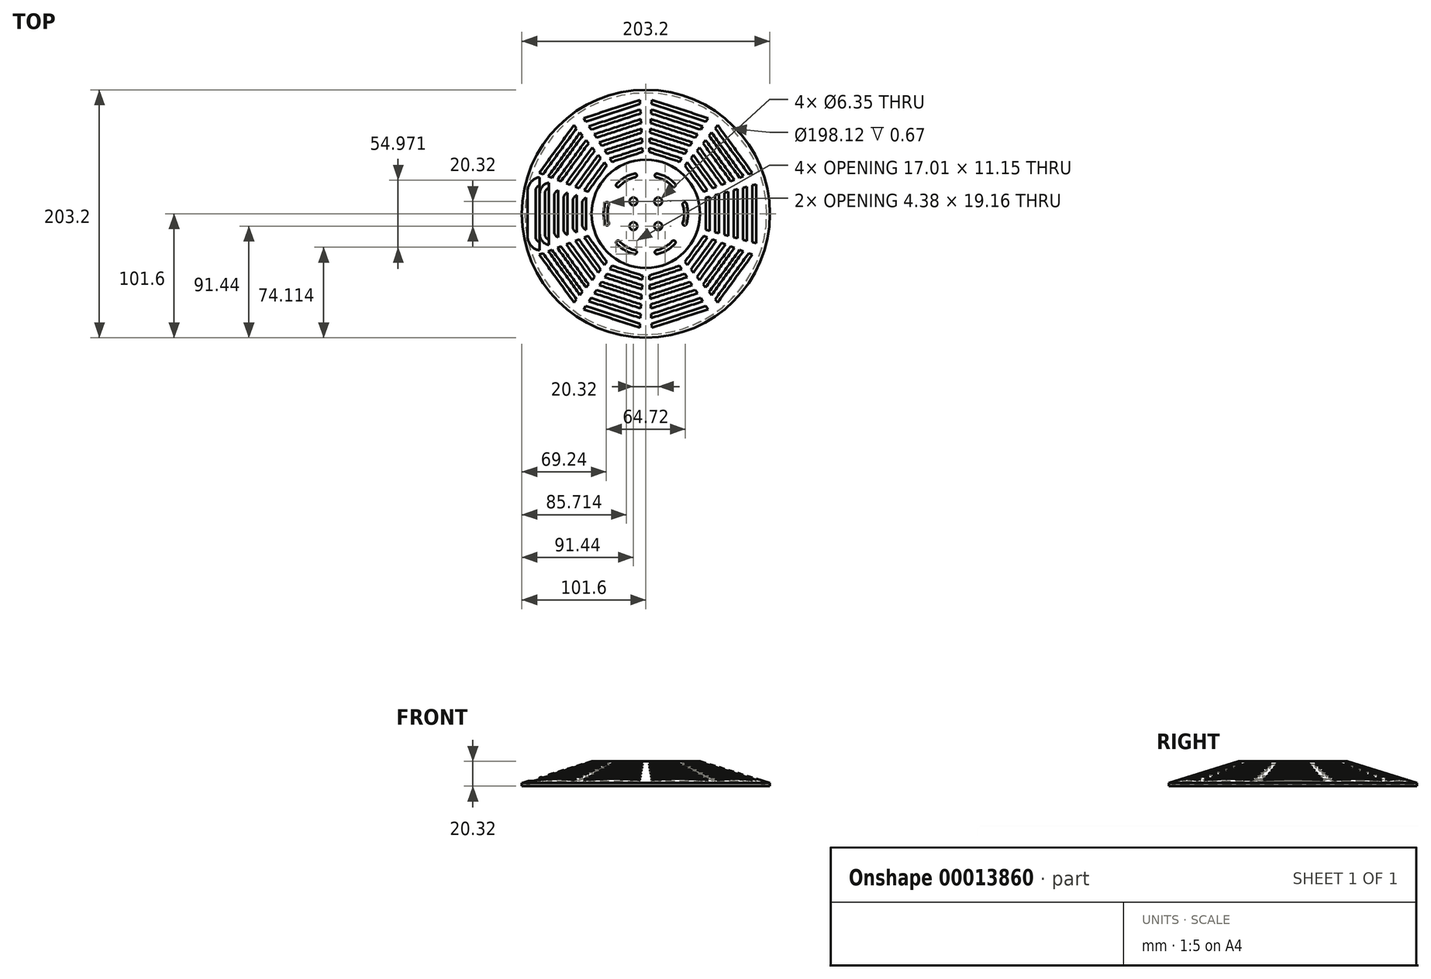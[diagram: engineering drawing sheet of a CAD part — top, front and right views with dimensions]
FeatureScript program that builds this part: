
annotation { "Feature Type Name" : "Feature", "Feature Type Description" : "" }
export const myFeature = defineFeature(function(context is Context, id is Id, definition is map)
    precondition{}
    {
        {
            var Q0;
            Q0=qCreatedBy(makeId("Front.planeOp"),FACE);
            var sketch = newSketch(context, id + "F0", { "sketchPlane" : qUnion([Q0])});
            skLineSegment(sketch, "E0", {"start": v(0, 0) * mm, "end": v(0, 20.32) * mm});
            skLineSegment(sketch, "E1", {"start": v(0, 20.32) * mm, "end": v(44.45, 20.32) * mm});
            skLineSegment(sketch, "E2", {"start": v(44.45, 20.32) * mm, "end": v(101.6, 2.54) * mm});
            skLineSegment(sketch, "E3", {"start": v(101.6, 2.54) * mm, "end": v(101.6, 0) * mm});
            skLineSegment(sketch, "E4", {"start": v(101.6, 0) * mm, "end": v(0, 0) * mm});
            skSolve(sketch);
        }
        {
            var Q0;
            Q0=makeQuery(id+"F0.imprint","IMPRINT",FACE,{"disambiguationData":[TD([[makeQuery(id+"F0.imprint","IMPRINT",EDGE,{"derivedFrom":sQuery(id+"F0.wireOp",EDGE,"E0")}),-1.0]])]});
            var Q1;
            Q1=sQuery(id+"F0.wireOp",EDGE,"E0");
            revolve(context, id + "F1", {"entities" : qUnion([Q0]), "axis" : qUnion([Q1]), "revolveType" : RevolveType.FULL});
        }
        {
            var Q0;
            Q0=makeQuery(id+"F1.opRevolve","SWEPT_FACE",FACE,{"disambiguationData":[OSD([sQuery(id+"F0.wireOp",EDGE,"E4")])]});
            shell(context, id + "F2", {"entities" : qUnion([Q0]), "thickness" : 2.54 * mm});
        }
        {
            var Q0;
            Q0=makeQuery(id+"F1.opRevolve","SWEPT_FACE",FACE,{"disambiguationData":[OSD([sQuery(id+"F0.wireOp",EDGE,"E1")])]});
            var sketch = newSketch(context, id + "F3", { "sketchPlane" : qUnion([Q0])});
            skArc(sketch, "E5", {"start": v(-30.23, 7.53) * mm, "mid": v(-31.38, 0) * mm, "end": v(-30.23, -7.53) * mm});
            skArc(sketch, "E6.0", {"start": v(-33.27, 8.47) * mm, "mid": v(-34.55, 0) * mm, "end": v(-33.27, -8.47) * mm});
            skArc(sketch, "E7", {"start": v(-33.27, -8.47) * mm, "mid": v(-31.28, -9.52) * mm, "end": v(-30.23, -7.53) * mm});
            skArc(sketch, "E8", {"start": v(-30.23, 7.53) * mm, "mid": v(-31.28, 9.52) * mm, "end": v(-33.27, 8.47) * mm});
            skSolve(sketch);
        }
        {
            var Q0;
            Q0=makeQuery(id+"F3.imprint","IMPRINT",FACE,{"disambiguationData":[TD([[makeQuery(id+"F3.imprint","IMPRINT",EDGE,{"derivedFrom":sQuery(id+"F3.wireOp",EDGE,"E5")}),-1.0]])]});
            extrude(context, id + "F4", {"entities" : qUnion([Q0]), "endBound" : BoundingType.THROUGH_ALL, "oppositeDirection" : true, "depth" : 25.4 * mm});
        }
        {
            var Q0;
            Q0=makeQuery(id+"F4.opExtrude","SWEPT_BODY",BODY,{"disambiguationData":[OSD([sQuery(id+"F3.wireOp",EDGE,"E5"),sQuery(id+"F3.wireOp",EDGE,"E6.0"),sQuery(id+"F3.wireOp",EDGE,"E7"),sQuery(id+"F3.wireOp",EDGE,"E8")])]});
            var Q1;
            Q1=makeQuery(id+"F1.opRevolve","SWEPT_EDGE",EDGE,{"disambiguationData":[OSD([sQuery(id+"F0.wireOp",EDGE,"E2"),sQuery(id+"F0.wireOp",EDGE,"E3")])]});
            circularPattern(context, id + "F5", {"entities" : qUnion([Q0]), "axis" : qUnion([Q1]), "angle" : 360 * degree, "instanceCount" : 6, "equalSpace" : true});
        }
        {
            var Q0;
            Q0=makeQuery(id+"F4.opExtrude","SWEPT_BODY",BODY,{"disambiguationData":[OSD([sQuery(id+"F3.wireOp",EDGE,"E5"),sQuery(id+"F3.wireOp",EDGE,"E6.0"),sQuery(id+"F3.wireOp",EDGE,"E7"),sQuery(id+"F3.wireOp",EDGE,"E8")])]});
            var Q1;
            Q1=makeQuery(id+"F5.opPattern","COPY",BODY,{"derivedFrom":makeQuery(id+"F4.opExtrude","SWEPT_BODY",BODY,{"disambiguationData":[OSD([sQuery(id+"F3.wireOp",EDGE,"E5"),sQuery(id+"F3.wireOp",EDGE,"E6.0"),sQuery(id+"F3.wireOp",EDGE,"E7"),sQuery(id+"F3.wireOp",EDGE,"E8")])]}),"instanceName":"1"});
            var Q2;
            Q2=makeQuery(id+"F5.opPattern","COPY",BODY,{"derivedFrom":makeQuery(id+"F4.opExtrude","SWEPT_BODY",BODY,{"disambiguationData":[OSD([sQuery(id+"F3.wireOp",EDGE,"E5"),sQuery(id+"F3.wireOp",EDGE,"E6.0"),sQuery(id+"F3.wireOp",EDGE,"E7"),sQuery(id+"F3.wireOp",EDGE,"E8")])]}),"instanceName":"2"});
            var Q3;
            Q3=makeQuery(id+"F5.opPattern","COPY",BODY,{"derivedFrom":makeQuery(id+"F4.opExtrude","SWEPT_BODY",BODY,{"disambiguationData":[OSD([sQuery(id+"F3.wireOp",EDGE,"E5"),sQuery(id+"F3.wireOp",EDGE,"E6.0"),sQuery(id+"F3.wireOp",EDGE,"E7"),sQuery(id+"F3.wireOp",EDGE,"E8")])]}),"instanceName":"3"});
            var Q4;
            Q4=makeQuery(id+"F5.opPattern","COPY",BODY,{"derivedFrom":makeQuery(id+"F4.opExtrude","SWEPT_BODY",BODY,{"disambiguationData":[OSD([sQuery(id+"F3.wireOp",EDGE,"E5"),sQuery(id+"F3.wireOp",EDGE,"E6.0"),sQuery(id+"F3.wireOp",EDGE,"E7"),sQuery(id+"F3.wireOp",EDGE,"E8")])]}),"instanceName":"4"});
            var Q5;
            Q5=makeQuery(id+"F5.opPattern","COPY",BODY,{"derivedFrom":makeQuery(id+"F4.opExtrude","SWEPT_BODY",BODY,{"disambiguationData":[OSD([sQuery(id+"F3.wireOp",EDGE,"E5"),sQuery(id+"F3.wireOp",EDGE,"E6.0"),sQuery(id+"F3.wireOp",EDGE,"E7"),sQuery(id+"F3.wireOp",EDGE,"E8")])]}),"instanceName":"5"});
            var Q6;
            Q6=makeQuery(id+"F1.opRevolve","SWEPT_BODY",BODY,{"disambiguationData":[OSD([sQuery(id+"F0.wireOp",EDGE,"E0"),sQuery(id+"F0.wireOp",EDGE,"E1"),sQuery(id+"F0.wireOp",EDGE,"E2"),sQuery(id+"F0.wireOp",EDGE,"E3"),sQuery(id+"F0.wireOp",EDGE,"E4")])]});
            booleanBodies(context, id + "F6", {"operationType" : BooleanOperationType.SUBTRACTION, "tools" : qUnion([Q0, Q1, Q2, Q3, Q4, Q5]), "targets" : qUnion([Q6])});
        }
        {
            var Q0;
            Q0=makeQuery(id+"F1.opRevolve","SWEPT_FACE",FACE,{"disambiguationData":[OSD([sQuery(id+"F0.wireOp",EDGE,"E1")])]});
            var sketch = newSketch(context, id + "F7", { "sketchPlane" : qUnion([Q0])});
            skLineSegment(sketch, "E9", {"start": v(0, 0) * mm, "end": v(-98.14, 26.3) * mm});
            skLineSegment(sketch, "E10", {"start": v(0, 0) * mm, "end": v(-98.14, -26.3) * mm});
            skLineSegment(sketch, "E11", {"start": v(-49.07, -13.15) * mm, "end": v(-49.07, 13.15) * mm});
            skLineSegment(sketch, "E12", {"start": v(-52.24, -14) * mm, "end": v(-52.24, 14) * mm});
            skLineSegment(sketch, "E13", {"start": v(-56.69, -15.19) * mm, "end": v(-56.69, 15.19) * mm});
            skLineSegment(sketch, "E14", {"start": v(-59.86, -16.04) * mm, "end": v(-59.86, 16.04) * mm});
            skLineSegment(sketch, "E15", {"start": v(-64.3, -17.23) * mm, "end": v(-64.3, 17.23) * mm});
            skLineSegment(sketch, "E16", {"start": v(-67.48, -18.08) * mm, "end": v(-67.48, 18.08) * mm});
            skLineSegment(sketch, "E17", {"start": v(-71.93, -19.27) * mm, "end": v(-71.93, 19.27) * mm});
            skLineSegment(sketch, "E18", {"start": v(-75.1, -20.12) * mm, "end": v(-75.1, 20.12) * mm});
            skLineSegment(sketch, "E19", {"start": v(-79.55, -21.32) * mm, "end": v(-79.55, 21.32) * mm});
            skLineSegment(sketch, "E20", {"start": v(-82.72, -22.17) * mm, "end": v(-82.72, 22.17) * mm});
            skLineSegment(sketch, "E21", {"start": v(-87.17, -23.36) * mm, "end": v(-87.17, 23.36) * mm});
            skLineSegment(sketch, "E22", {"start": v(-90.34, -24.2) * mm, "end": v(-90.34, 24.2) * mm});
            skSolve(sketch);
        }
        {
            var Q0;
            {var subQ1=sQuery(id+"F7.wireOp",EDGE,"E19");Q0=makeQuery(id+"F7.imprint","IMPRINT",FACE,{"disambiguationData":[TD([[makeQuery(id+"F7.imprint","IMPRINT",EDGE,{"derivedFrom":subQ1}),1.0]])]});}
            var Q1;
            {var subQ1=sQuery(id+"F7.wireOp",EDGE,"E17");Q1=makeQuery(id+"F7.imprint","IMPRINT",FACE,{"disambiguationData":[TD([[makeQuery(id+"F7.imprint","IMPRINT",EDGE,{"derivedFrom":subQ1}),1.0]])]});}
            var Q2;
            {var subQ1=sQuery(id+"F7.wireOp",EDGE,"E15");Q2=makeQuery(id+"F7.imprint","IMPRINT",FACE,{"disambiguationData":[TD([[makeQuery(id+"F7.imprint","IMPRINT",EDGE,{"derivedFrom":subQ1}),1.0]])]});}
            var Q3;
            {var subQ1=sQuery(id+"F7.wireOp",EDGE,"E13");Q3=makeQuery(id+"F7.imprint","IMPRINT",FACE,{"disambiguationData":[TD([[makeQuery(id+"F7.imprint","IMPRINT",EDGE,{"derivedFrom":subQ1}),1.0]])]});}
            var Q4;
            {var subQ1=sQuery(id+"F7.wireOp",EDGE,"E11");Q4=makeQuery(id+"F7.imprint","IMPRINT",FACE,{"disambiguationData":[TD([[makeQuery(id+"F7.imprint","IMPRINT",EDGE,{"derivedFrom":subQ1}),1.0]])]});}
            var Q5;
            {var subQ1=sQuery(id+"F7.wireOp",EDGE,"E21");Q5=makeQuery(id+"F7.imprint","IMPRINT",FACE,{"disambiguationData":[TD([[makeQuery(id+"F7.imprint","IMPRINT",EDGE,{"derivedFrom":subQ1}),1.0]])]});}
            extrude(context, id + "F8", {"entities" : qUnion([Q0, Q1, Q2, Q3, Q4, Q5]), "oppositeDirection" : true, "depth" : 25.4 * mm});
        }
        {
            var Q0;
            Q0=makeQuery(id+"F8.opExtrude","SWEPT_BODY",BODY,{"disambiguationData":[OSD([sQuery(id+"F7.wireOp",EDGE,"E9"),sQuery(id+"F7.wireOp",EDGE,"E10"),sQuery(id+"F7.wireOp",EDGE,"E21"),sQuery(id+"F7.wireOp",EDGE,"E22")])]});
            var Q1;
            Q1=makeQuery(id+"F8.opExtrude","SWEPT_BODY",BODY,{"disambiguationData":[OSD([sQuery(id+"F7.wireOp",EDGE,"E9"),sQuery(id+"F7.wireOp",EDGE,"E10"),sQuery(id+"F7.wireOp",EDGE,"E19"),sQuery(id+"F7.wireOp",EDGE,"E20")])]});
            var Q2;
            Q2=makeQuery(id+"F8.opExtrude","SWEPT_BODY",BODY,{"disambiguationData":[OSD([sQuery(id+"F7.wireOp",EDGE,"E9"),sQuery(id+"F7.wireOp",EDGE,"E10"),sQuery(id+"F7.wireOp",EDGE,"E17"),sQuery(id+"F7.wireOp",EDGE,"E18")])]});
            var Q3;
            Q3=makeQuery(id+"F8.opExtrude","SWEPT_BODY",BODY,{"disambiguationData":[OSD([sQuery(id+"F7.wireOp",EDGE,"E9"),sQuery(id+"F7.wireOp",EDGE,"E10"),sQuery(id+"F7.wireOp",EDGE,"E15"),sQuery(id+"F7.wireOp",EDGE,"E16")])]});
            var Q4;
            Q4=makeQuery(id+"F8.opExtrude","SWEPT_BODY",BODY,{"disambiguationData":[OSD([sQuery(id+"F7.wireOp",EDGE,"E9"),sQuery(id+"F7.wireOp",EDGE,"E10"),sQuery(id+"F7.wireOp",EDGE,"E13"),sQuery(id+"F7.wireOp",EDGE,"E14")])]});
            var Q5;
            Q5=makeQuery(id+"F8.opExtrude","SWEPT_BODY",BODY,{"disambiguationData":[OSD([sQuery(id+"F7.wireOp",EDGE,"E9"),sQuery(id+"F7.wireOp",EDGE,"E10"),sQuery(id+"F7.wireOp",EDGE,"E11"),sQuery(id+"F7.wireOp",EDGE,"E12")])]});
            var Q6;
            Q6=makeQuery(id+"F1.opRevolve","SWEPT_EDGE",EDGE,{"disambiguationData":[OSD([sQuery(id+"F0.wireOp",EDGE,"E2"),sQuery(id+"F0.wireOp",EDGE,"E3")])]});
            circularPattern(context, id + "F9", {"entities" : qUnion([Q0, Q1, Q2, Q3, Q4, Q5]), "axis" : qUnion([Q6]), "angle" : 360 * degree, "instanceCount" : 10, "equalSpace" : true});
        }
        {
            var Q0;
            Q0=makeQuery(id+"F8.opExtrude","SWEPT_BODY",BODY,{"disambiguationData":[OSD([sQuery(id+"F7.wireOp",EDGE,"E9"),sQuery(id+"F7.wireOp",EDGE,"E10"),sQuery(id+"F7.wireOp",EDGE,"E21"),sQuery(id+"F7.wireOp",EDGE,"E22")])]});
            var Q1;
            Q1=makeQuery(id+"F8.opExtrude","SWEPT_BODY",BODY,{"disambiguationData":[OSD([sQuery(id+"F7.wireOp",EDGE,"E9"),sQuery(id+"F7.wireOp",EDGE,"E10"),sQuery(id+"F7.wireOp",EDGE,"E11"),sQuery(id+"F7.wireOp",EDGE,"E12")])]});
            var Q2;
            Q2=makeQuery(id+"F8.opExtrude","SWEPT_BODY",BODY,{"disambiguationData":[OSD([sQuery(id+"F7.wireOp",EDGE,"E9"),sQuery(id+"F7.wireOp",EDGE,"E10"),sQuery(id+"F7.wireOp",EDGE,"E13"),sQuery(id+"F7.wireOp",EDGE,"E14")])]});
            var Q3;
            Q3=makeQuery(id+"F8.opExtrude","SWEPT_BODY",BODY,{"disambiguationData":[OSD([sQuery(id+"F7.wireOp",EDGE,"E9"),sQuery(id+"F7.wireOp",EDGE,"E10"),sQuery(id+"F7.wireOp",EDGE,"E15"),sQuery(id+"F7.wireOp",EDGE,"E16")])]});
            var Q4;
            Q4=makeQuery(id+"F8.opExtrude","SWEPT_BODY",BODY,{"disambiguationData":[OSD([sQuery(id+"F7.wireOp",EDGE,"E9"),sQuery(id+"F7.wireOp",EDGE,"E10"),sQuery(id+"F7.wireOp",EDGE,"E17"),sQuery(id+"F7.wireOp",EDGE,"E18")])]});
            var Q5;
            Q5=makeQuery(id+"F8.opExtrude","SWEPT_BODY",BODY,{"disambiguationData":[OSD([sQuery(id+"F7.wireOp",EDGE,"E9"),sQuery(id+"F7.wireOp",EDGE,"E10"),sQuery(id+"F7.wireOp",EDGE,"E19"),sQuery(id+"F7.wireOp",EDGE,"E20")])]});
            var Q6;
            Q6=makeQuery(id+"F9.opPattern","COPY",BODY,{"derivedFrom":makeQuery(id+"F8.opExtrude","SWEPT_BODY",BODY,{"disambiguationData":[OSD([sQuery(id+"F7.wireOp",EDGE,"E9"),sQuery(id+"F7.wireOp",EDGE,"E10"),sQuery(id+"F7.wireOp",EDGE,"E21"),sQuery(id+"F7.wireOp",EDGE,"E22")])]}),"instanceName":"1"});
            var Q7;
            Q7=makeQuery(id+"F9.opPattern","COPY",BODY,{"derivedFrom":makeQuery(id+"F8.opExtrude","SWEPT_BODY",BODY,{"disambiguationData":[OSD([sQuery(id+"F7.wireOp",EDGE,"E9"),sQuery(id+"F7.wireOp",EDGE,"E10"),sQuery(id+"F7.wireOp",EDGE,"E11"),sQuery(id+"F7.wireOp",EDGE,"E12")])]}),"instanceName":"1"});
            var Q8;
            Q8=makeQuery(id+"F9.opPattern","COPY",BODY,{"derivedFrom":makeQuery(id+"F8.opExtrude","SWEPT_BODY",BODY,{"disambiguationData":[OSD([sQuery(id+"F7.wireOp",EDGE,"E9"),sQuery(id+"F7.wireOp",EDGE,"E10"),sQuery(id+"F7.wireOp",EDGE,"E13"),sQuery(id+"F7.wireOp",EDGE,"E14")])]}),"instanceName":"1"});
            var Q9;
            Q9=makeQuery(id+"F9.opPattern","COPY",BODY,{"derivedFrom":makeQuery(id+"F8.opExtrude","SWEPT_BODY",BODY,{"disambiguationData":[OSD([sQuery(id+"F7.wireOp",EDGE,"E9"),sQuery(id+"F7.wireOp",EDGE,"E10"),sQuery(id+"F7.wireOp",EDGE,"E15"),sQuery(id+"F7.wireOp",EDGE,"E16")])]}),"instanceName":"1"});
            var Q10;
            Q10=makeQuery(id+"F9.opPattern","COPY",BODY,{"derivedFrom":makeQuery(id+"F8.opExtrude","SWEPT_BODY",BODY,{"disambiguationData":[OSD([sQuery(id+"F7.wireOp",EDGE,"E9"),sQuery(id+"F7.wireOp",EDGE,"E10"),sQuery(id+"F7.wireOp",EDGE,"E17"),sQuery(id+"F7.wireOp",EDGE,"E18")])]}),"instanceName":"1"});
            var Q11;
            Q11=makeQuery(id+"F9.opPattern","COPY",BODY,{"derivedFrom":makeQuery(id+"F8.opExtrude","SWEPT_BODY",BODY,{"disambiguationData":[OSD([sQuery(id+"F7.wireOp",EDGE,"E9"),sQuery(id+"F7.wireOp",EDGE,"E10"),sQuery(id+"F7.wireOp",EDGE,"E19"),sQuery(id+"F7.wireOp",EDGE,"E20")])]}),"instanceName":"1"});
            var Q12;
            Q12=makeQuery(id+"F9.opPattern","COPY",BODY,{"derivedFrom":makeQuery(id+"F8.opExtrude","SWEPT_BODY",BODY,{"disambiguationData":[OSD([sQuery(id+"F7.wireOp",EDGE,"E9"),sQuery(id+"F7.wireOp",EDGE,"E10"),sQuery(id+"F7.wireOp",EDGE,"E21"),sQuery(id+"F7.wireOp",EDGE,"E22")])]}),"instanceName":"2"});
            var Q13;
            Q13=makeQuery(id+"F9.opPattern","COPY",BODY,{"derivedFrom":makeQuery(id+"F8.opExtrude","SWEPT_BODY",BODY,{"disambiguationData":[OSD([sQuery(id+"F7.wireOp",EDGE,"E9"),sQuery(id+"F7.wireOp",EDGE,"E10"),sQuery(id+"F7.wireOp",EDGE,"E11"),sQuery(id+"F7.wireOp",EDGE,"E12")])]}),"instanceName":"2"});
            var Q14;
            Q14=makeQuery(id+"F9.opPattern","COPY",BODY,{"derivedFrom":makeQuery(id+"F8.opExtrude","SWEPT_BODY",BODY,{"disambiguationData":[OSD([sQuery(id+"F7.wireOp",EDGE,"E9"),sQuery(id+"F7.wireOp",EDGE,"E10"),sQuery(id+"F7.wireOp",EDGE,"E13"),sQuery(id+"F7.wireOp",EDGE,"E14")])]}),"instanceName":"2"});
            var Q15;
            Q15=makeQuery(id+"F9.opPattern","COPY",BODY,{"derivedFrom":makeQuery(id+"F8.opExtrude","SWEPT_BODY",BODY,{"disambiguationData":[OSD([sQuery(id+"F7.wireOp",EDGE,"E9"),sQuery(id+"F7.wireOp",EDGE,"E10"),sQuery(id+"F7.wireOp",EDGE,"E15"),sQuery(id+"F7.wireOp",EDGE,"E16")])]}),"instanceName":"2"});
            var Q16;
            Q16=makeQuery(id+"F9.opPattern","COPY",BODY,{"derivedFrom":makeQuery(id+"F8.opExtrude","SWEPT_BODY",BODY,{"disambiguationData":[OSD([sQuery(id+"F7.wireOp",EDGE,"E9"),sQuery(id+"F7.wireOp",EDGE,"E10"),sQuery(id+"F7.wireOp",EDGE,"E17"),sQuery(id+"F7.wireOp",EDGE,"E18")])]}),"instanceName":"2"});
            var Q17;
            Q17=makeQuery(id+"F9.opPattern","COPY",BODY,{"derivedFrom":makeQuery(id+"F8.opExtrude","SWEPT_BODY",BODY,{"disambiguationData":[OSD([sQuery(id+"F7.wireOp",EDGE,"E9"),sQuery(id+"F7.wireOp",EDGE,"E10"),sQuery(id+"F7.wireOp",EDGE,"E19"),sQuery(id+"F7.wireOp",EDGE,"E20")])]}),"instanceName":"2"});
            var Q18;
            Q18=makeQuery(id+"F9.opPattern","COPY",BODY,{"derivedFrom":makeQuery(id+"F8.opExtrude","SWEPT_BODY",BODY,{"disambiguationData":[OSD([sQuery(id+"F7.wireOp",EDGE,"E9"),sQuery(id+"F7.wireOp",EDGE,"E10"),sQuery(id+"F7.wireOp",EDGE,"E21"),sQuery(id+"F7.wireOp",EDGE,"E22")])]}),"instanceName":"3"});
            var Q19;
            Q19=makeQuery(id+"F9.opPattern","COPY",BODY,{"derivedFrom":makeQuery(id+"F8.opExtrude","SWEPT_BODY",BODY,{"disambiguationData":[OSD([sQuery(id+"F7.wireOp",EDGE,"E9"),sQuery(id+"F7.wireOp",EDGE,"E10"),sQuery(id+"F7.wireOp",EDGE,"E11"),sQuery(id+"F7.wireOp",EDGE,"E12")])]}),"instanceName":"3"});
            var Q20;
            Q20=makeQuery(id+"F9.opPattern","COPY",BODY,{"derivedFrom":makeQuery(id+"F8.opExtrude","SWEPT_BODY",BODY,{"disambiguationData":[OSD([sQuery(id+"F7.wireOp",EDGE,"E9"),sQuery(id+"F7.wireOp",EDGE,"E10"),sQuery(id+"F7.wireOp",EDGE,"E13"),sQuery(id+"F7.wireOp",EDGE,"E14")])]}),"instanceName":"3"});
            var Q21;
            Q21=makeQuery(id+"F9.opPattern","COPY",BODY,{"derivedFrom":makeQuery(id+"F8.opExtrude","SWEPT_BODY",BODY,{"disambiguationData":[OSD([sQuery(id+"F7.wireOp",EDGE,"E9"),sQuery(id+"F7.wireOp",EDGE,"E10"),sQuery(id+"F7.wireOp",EDGE,"E15"),sQuery(id+"F7.wireOp",EDGE,"E16")])]}),"instanceName":"3"});
            var Q22;
            Q22=makeQuery(id+"F9.opPattern","COPY",BODY,{"derivedFrom":makeQuery(id+"F8.opExtrude","SWEPT_BODY",BODY,{"disambiguationData":[OSD([sQuery(id+"F7.wireOp",EDGE,"E9"),sQuery(id+"F7.wireOp",EDGE,"E10"),sQuery(id+"F7.wireOp",EDGE,"E17"),sQuery(id+"F7.wireOp",EDGE,"E18")])]}),"instanceName":"3"});
            var Q23;
            Q23=makeQuery(id+"F9.opPattern","COPY",BODY,{"derivedFrom":makeQuery(id+"F8.opExtrude","SWEPT_BODY",BODY,{"disambiguationData":[OSD([sQuery(id+"F7.wireOp",EDGE,"E9"),sQuery(id+"F7.wireOp",EDGE,"E10"),sQuery(id+"F7.wireOp",EDGE,"E19"),sQuery(id+"F7.wireOp",EDGE,"E20")])]}),"instanceName":"3"});
            var Q24;
            Q24=makeQuery(id+"F9.opPattern","COPY",BODY,{"derivedFrom":makeQuery(id+"F8.opExtrude","SWEPT_BODY",BODY,{"disambiguationData":[OSD([sQuery(id+"F7.wireOp",EDGE,"E9"),sQuery(id+"F7.wireOp",EDGE,"E10"),sQuery(id+"F7.wireOp",EDGE,"E21"),sQuery(id+"F7.wireOp",EDGE,"E22")])]}),"instanceName":"4"});
            var Q25;
            Q25=makeQuery(id+"F9.opPattern","COPY",BODY,{"derivedFrom":makeQuery(id+"F8.opExtrude","SWEPT_BODY",BODY,{"disambiguationData":[OSD([sQuery(id+"F7.wireOp",EDGE,"E9"),sQuery(id+"F7.wireOp",EDGE,"E10"),sQuery(id+"F7.wireOp",EDGE,"E11"),sQuery(id+"F7.wireOp",EDGE,"E12")])]}),"instanceName":"4"});
            var Q26;
            Q26=makeQuery(id+"F9.opPattern","COPY",BODY,{"derivedFrom":makeQuery(id+"F8.opExtrude","SWEPT_BODY",BODY,{"disambiguationData":[OSD([sQuery(id+"F7.wireOp",EDGE,"E9"),sQuery(id+"F7.wireOp",EDGE,"E10"),sQuery(id+"F7.wireOp",EDGE,"E13"),sQuery(id+"F7.wireOp",EDGE,"E14")])]}),"instanceName":"4"});
            var Q27;
            Q27=makeQuery(id+"F9.opPattern","COPY",BODY,{"derivedFrom":makeQuery(id+"F8.opExtrude","SWEPT_BODY",BODY,{"disambiguationData":[OSD([sQuery(id+"F7.wireOp",EDGE,"E9"),sQuery(id+"F7.wireOp",EDGE,"E10"),sQuery(id+"F7.wireOp",EDGE,"E15"),sQuery(id+"F7.wireOp",EDGE,"E16")])]}),"instanceName":"4"});
            var Q28;
            Q28=makeQuery(id+"F9.opPattern","COPY",BODY,{"derivedFrom":makeQuery(id+"F8.opExtrude","SWEPT_BODY",BODY,{"disambiguationData":[OSD([sQuery(id+"F7.wireOp",EDGE,"E9"),sQuery(id+"F7.wireOp",EDGE,"E10"),sQuery(id+"F7.wireOp",EDGE,"E17"),sQuery(id+"F7.wireOp",EDGE,"E18")])]}),"instanceName":"4"});
            var Q29;
            Q29=makeQuery(id+"F9.opPattern","COPY",BODY,{"derivedFrom":makeQuery(id+"F8.opExtrude","SWEPT_BODY",BODY,{"disambiguationData":[OSD([sQuery(id+"F7.wireOp",EDGE,"E9"),sQuery(id+"F7.wireOp",EDGE,"E10"),sQuery(id+"F7.wireOp",EDGE,"E19"),sQuery(id+"F7.wireOp",EDGE,"E20")])]}),"instanceName":"4"});
            var Q30;
            Q30=makeQuery(id+"F9.opPattern","COPY",BODY,{"derivedFrom":makeQuery(id+"F8.opExtrude","SWEPT_BODY",BODY,{"disambiguationData":[OSD([sQuery(id+"F7.wireOp",EDGE,"E9"),sQuery(id+"F7.wireOp",EDGE,"E10"),sQuery(id+"F7.wireOp",EDGE,"E21"),sQuery(id+"F7.wireOp",EDGE,"E22")])]}),"instanceName":"5"});
            var Q31;
            Q31=makeQuery(id+"F9.opPattern","COPY",BODY,{"derivedFrom":makeQuery(id+"F8.opExtrude","SWEPT_BODY",BODY,{"disambiguationData":[OSD([sQuery(id+"F7.wireOp",EDGE,"E9"),sQuery(id+"F7.wireOp",EDGE,"E10"),sQuery(id+"F7.wireOp",EDGE,"E11"),sQuery(id+"F7.wireOp",EDGE,"E12")])]}),"instanceName":"5"});
            var Q32;
            Q32=makeQuery(id+"F9.opPattern","COPY",BODY,{"derivedFrom":makeQuery(id+"F8.opExtrude","SWEPT_BODY",BODY,{"disambiguationData":[OSD([sQuery(id+"F7.wireOp",EDGE,"E9"),sQuery(id+"F7.wireOp",EDGE,"E10"),sQuery(id+"F7.wireOp",EDGE,"E13"),sQuery(id+"F7.wireOp",EDGE,"E14")])]}),"instanceName":"5"});
            var Q33;
            Q33=makeQuery(id+"F9.opPattern","COPY",BODY,{"derivedFrom":makeQuery(id+"F8.opExtrude","SWEPT_BODY",BODY,{"disambiguationData":[OSD([sQuery(id+"F7.wireOp",EDGE,"E9"),sQuery(id+"F7.wireOp",EDGE,"E10"),sQuery(id+"F7.wireOp",EDGE,"E15"),sQuery(id+"F7.wireOp",EDGE,"E16")])]}),"instanceName":"5"});
            var Q34;
            Q34=makeQuery(id+"F9.opPattern","COPY",BODY,{"derivedFrom":makeQuery(id+"F8.opExtrude","SWEPT_BODY",BODY,{"disambiguationData":[OSD([sQuery(id+"F7.wireOp",EDGE,"E9"),sQuery(id+"F7.wireOp",EDGE,"E10"),sQuery(id+"F7.wireOp",EDGE,"E17"),sQuery(id+"F7.wireOp",EDGE,"E18")])]}),"instanceName":"5"});
            var Q35;
            Q35=makeQuery(id+"F9.opPattern","COPY",BODY,{"derivedFrom":makeQuery(id+"F8.opExtrude","SWEPT_BODY",BODY,{"disambiguationData":[OSD([sQuery(id+"F7.wireOp",EDGE,"E9"),sQuery(id+"F7.wireOp",EDGE,"E10"),sQuery(id+"F7.wireOp",EDGE,"E19"),sQuery(id+"F7.wireOp",EDGE,"E20")])]}),"instanceName":"5"});
            var Q36;
            Q36=makeQuery(id+"F9.opPattern","COPY",BODY,{"derivedFrom":makeQuery(id+"F8.opExtrude","SWEPT_BODY",BODY,{"disambiguationData":[OSD([sQuery(id+"F7.wireOp",EDGE,"E9"),sQuery(id+"F7.wireOp",EDGE,"E10"),sQuery(id+"F7.wireOp",EDGE,"E21"),sQuery(id+"F7.wireOp",EDGE,"E22")])]}),"instanceName":"6"});
            var Q37;
            Q37=makeQuery(id+"F9.opPattern","COPY",BODY,{"derivedFrom":makeQuery(id+"F8.opExtrude","SWEPT_BODY",BODY,{"disambiguationData":[OSD([sQuery(id+"F7.wireOp",EDGE,"E9"),sQuery(id+"F7.wireOp",EDGE,"E10"),sQuery(id+"F7.wireOp",EDGE,"E11"),sQuery(id+"F7.wireOp",EDGE,"E12")])]}),"instanceName":"6"});
            var Q38;
            Q38=makeQuery(id+"F9.opPattern","COPY",BODY,{"derivedFrom":makeQuery(id+"F8.opExtrude","SWEPT_BODY",BODY,{"disambiguationData":[OSD([sQuery(id+"F7.wireOp",EDGE,"E9"),sQuery(id+"F7.wireOp",EDGE,"E10"),sQuery(id+"F7.wireOp",EDGE,"E13"),sQuery(id+"F7.wireOp",EDGE,"E14")])]}),"instanceName":"6"});
            var Q39;
            Q39=makeQuery(id+"F9.opPattern","COPY",BODY,{"derivedFrom":makeQuery(id+"F8.opExtrude","SWEPT_BODY",BODY,{"disambiguationData":[OSD([sQuery(id+"F7.wireOp",EDGE,"E9"),sQuery(id+"F7.wireOp",EDGE,"E10"),sQuery(id+"F7.wireOp",EDGE,"E15"),sQuery(id+"F7.wireOp",EDGE,"E16")])]}),"instanceName":"6"});
            var Q40;
            Q40=makeQuery(id+"F9.opPattern","COPY",BODY,{"derivedFrom":makeQuery(id+"F8.opExtrude","SWEPT_BODY",BODY,{"disambiguationData":[OSD([sQuery(id+"F7.wireOp",EDGE,"E9"),sQuery(id+"F7.wireOp",EDGE,"E10"),sQuery(id+"F7.wireOp",EDGE,"E17"),sQuery(id+"F7.wireOp",EDGE,"E18")])]}),"instanceName":"6"});
            var Q41;
            Q41=makeQuery(id+"F9.opPattern","COPY",BODY,{"derivedFrom":makeQuery(id+"F8.opExtrude","SWEPT_BODY",BODY,{"disambiguationData":[OSD([sQuery(id+"F7.wireOp",EDGE,"E9"),sQuery(id+"F7.wireOp",EDGE,"E10"),sQuery(id+"F7.wireOp",EDGE,"E19"),sQuery(id+"F7.wireOp",EDGE,"E20")])]}),"instanceName":"6"});
            var Q42;
            Q42=makeQuery(id+"F9.opPattern","COPY",BODY,{"derivedFrom":makeQuery(id+"F8.opExtrude","SWEPT_BODY",BODY,{"disambiguationData":[OSD([sQuery(id+"F7.wireOp",EDGE,"E9"),sQuery(id+"F7.wireOp",EDGE,"E10"),sQuery(id+"F7.wireOp",EDGE,"E21"),sQuery(id+"F7.wireOp",EDGE,"E22")])]}),"instanceName":"7"});
            var Q43;
            Q43=makeQuery(id+"F9.opPattern","COPY",BODY,{"derivedFrom":makeQuery(id+"F8.opExtrude","SWEPT_BODY",BODY,{"disambiguationData":[OSD([sQuery(id+"F7.wireOp",EDGE,"E9"),sQuery(id+"F7.wireOp",EDGE,"E10"),sQuery(id+"F7.wireOp",EDGE,"E11"),sQuery(id+"F7.wireOp",EDGE,"E12")])]}),"instanceName":"7"});
            var Q44;
            Q44=makeQuery(id+"F9.opPattern","COPY",BODY,{"derivedFrom":makeQuery(id+"F8.opExtrude","SWEPT_BODY",BODY,{"disambiguationData":[OSD([sQuery(id+"F7.wireOp",EDGE,"E9"),sQuery(id+"F7.wireOp",EDGE,"E10"),sQuery(id+"F7.wireOp",EDGE,"E13"),sQuery(id+"F7.wireOp",EDGE,"E14")])]}),"instanceName":"7"});
            var Q45;
            Q45=makeQuery(id+"F9.opPattern","COPY",BODY,{"derivedFrom":makeQuery(id+"F8.opExtrude","SWEPT_BODY",BODY,{"disambiguationData":[OSD([sQuery(id+"F7.wireOp",EDGE,"E9"),sQuery(id+"F7.wireOp",EDGE,"E10"),sQuery(id+"F7.wireOp",EDGE,"E15"),sQuery(id+"F7.wireOp",EDGE,"E16")])]}),"instanceName":"7"});
            var Q46;
            Q46=makeQuery(id+"F9.opPattern","COPY",BODY,{"derivedFrom":makeQuery(id+"F8.opExtrude","SWEPT_BODY",BODY,{"disambiguationData":[OSD([sQuery(id+"F7.wireOp",EDGE,"E9"),sQuery(id+"F7.wireOp",EDGE,"E10"),sQuery(id+"F7.wireOp",EDGE,"E17"),sQuery(id+"F7.wireOp",EDGE,"E18")])]}),"instanceName":"7"});
            var Q47;
            Q47=makeQuery(id+"F9.opPattern","COPY",BODY,{"derivedFrom":makeQuery(id+"F8.opExtrude","SWEPT_BODY",BODY,{"disambiguationData":[OSD([sQuery(id+"F7.wireOp",EDGE,"E9"),sQuery(id+"F7.wireOp",EDGE,"E10"),sQuery(id+"F7.wireOp",EDGE,"E19"),sQuery(id+"F7.wireOp",EDGE,"E20")])]}),"instanceName":"7"});
            var Q48;
            Q48=makeQuery(id+"F9.opPattern","COPY",BODY,{"derivedFrom":makeQuery(id+"F8.opExtrude","SWEPT_BODY",BODY,{"disambiguationData":[OSD([sQuery(id+"F7.wireOp",EDGE,"E9"),sQuery(id+"F7.wireOp",EDGE,"E10"),sQuery(id+"F7.wireOp",EDGE,"E21"),sQuery(id+"F7.wireOp",EDGE,"E22")])]}),"instanceName":"8"});
            var Q49;
            Q49=makeQuery(id+"F9.opPattern","COPY",BODY,{"derivedFrom":makeQuery(id+"F8.opExtrude","SWEPT_BODY",BODY,{"disambiguationData":[OSD([sQuery(id+"F7.wireOp",EDGE,"E9"),sQuery(id+"F7.wireOp",EDGE,"E10"),sQuery(id+"F7.wireOp",EDGE,"E11"),sQuery(id+"F7.wireOp",EDGE,"E12")])]}),"instanceName":"8"});
            var Q50;
            Q50=makeQuery(id+"F9.opPattern","COPY",BODY,{"derivedFrom":makeQuery(id+"F8.opExtrude","SWEPT_BODY",BODY,{"disambiguationData":[OSD([sQuery(id+"F7.wireOp",EDGE,"E9"),sQuery(id+"F7.wireOp",EDGE,"E10"),sQuery(id+"F7.wireOp",EDGE,"E13"),sQuery(id+"F7.wireOp",EDGE,"E14")])]}),"instanceName":"8"});
            var Q51;
            Q51=makeQuery(id+"F9.opPattern","COPY",BODY,{"derivedFrom":makeQuery(id+"F8.opExtrude","SWEPT_BODY",BODY,{"disambiguationData":[OSD([sQuery(id+"F7.wireOp",EDGE,"E9"),sQuery(id+"F7.wireOp",EDGE,"E10"),sQuery(id+"F7.wireOp",EDGE,"E15"),sQuery(id+"F7.wireOp",EDGE,"E16")])]}),"instanceName":"8"});
            var Q52;
            Q52=makeQuery(id+"F9.opPattern","COPY",BODY,{"derivedFrom":makeQuery(id+"F8.opExtrude","SWEPT_BODY",BODY,{"disambiguationData":[OSD([sQuery(id+"F7.wireOp",EDGE,"E9"),sQuery(id+"F7.wireOp",EDGE,"E10"),sQuery(id+"F7.wireOp",EDGE,"E17"),sQuery(id+"F7.wireOp",EDGE,"E18")])]}),"instanceName":"8"});
            var Q53;
            Q53=makeQuery(id+"F9.opPattern","COPY",BODY,{"derivedFrom":makeQuery(id+"F8.opExtrude","SWEPT_BODY",BODY,{"disambiguationData":[OSD([sQuery(id+"F7.wireOp",EDGE,"E9"),sQuery(id+"F7.wireOp",EDGE,"E10"),sQuery(id+"F7.wireOp",EDGE,"E19"),sQuery(id+"F7.wireOp",EDGE,"E20")])]}),"instanceName":"8"});
            var Q54;
            Q54=makeQuery(id+"F9.opPattern","COPY",BODY,{"derivedFrom":makeQuery(id+"F8.opExtrude","SWEPT_BODY",BODY,{"disambiguationData":[OSD([sQuery(id+"F7.wireOp",EDGE,"E9"),sQuery(id+"F7.wireOp",EDGE,"E10"),sQuery(id+"F7.wireOp",EDGE,"E21"),sQuery(id+"F7.wireOp",EDGE,"E22")])]}),"instanceName":"9"});
            var Q55;
            Q55=makeQuery(id+"F9.opPattern","COPY",BODY,{"derivedFrom":makeQuery(id+"F8.opExtrude","SWEPT_BODY",BODY,{"disambiguationData":[OSD([sQuery(id+"F7.wireOp",EDGE,"E9"),sQuery(id+"F7.wireOp",EDGE,"E10"),sQuery(id+"F7.wireOp",EDGE,"E11"),sQuery(id+"F7.wireOp",EDGE,"E12")])]}),"instanceName":"9"});
            var Q56;
            Q56=makeQuery(id+"F9.opPattern","COPY",BODY,{"derivedFrom":makeQuery(id+"F8.opExtrude","SWEPT_BODY",BODY,{"disambiguationData":[OSD([sQuery(id+"F7.wireOp",EDGE,"E9"),sQuery(id+"F7.wireOp",EDGE,"E10"),sQuery(id+"F7.wireOp",EDGE,"E13"),sQuery(id+"F7.wireOp",EDGE,"E14")])]}),"instanceName":"9"});
            var Q57;
            Q57=makeQuery(id+"F9.opPattern","COPY",BODY,{"derivedFrom":makeQuery(id+"F8.opExtrude","SWEPT_BODY",BODY,{"disambiguationData":[OSD([sQuery(id+"F7.wireOp",EDGE,"E9"),sQuery(id+"F7.wireOp",EDGE,"E10"),sQuery(id+"F7.wireOp",EDGE,"E15"),sQuery(id+"F7.wireOp",EDGE,"E16")])]}),"instanceName":"9"});
            var Q58;
            Q58=makeQuery(id+"F9.opPattern","COPY",BODY,{"derivedFrom":makeQuery(id+"F8.opExtrude","SWEPT_BODY",BODY,{"disambiguationData":[OSD([sQuery(id+"F7.wireOp",EDGE,"E9"),sQuery(id+"F7.wireOp",EDGE,"E10"),sQuery(id+"F7.wireOp",EDGE,"E17"),sQuery(id+"F7.wireOp",EDGE,"E18")])]}),"instanceName":"9"});
            var Q59;
            Q59=makeQuery(id+"F9.opPattern","COPY",BODY,{"derivedFrom":makeQuery(id+"F8.opExtrude","SWEPT_BODY",BODY,{"disambiguationData":[OSD([sQuery(id+"F7.wireOp",EDGE,"E9"),sQuery(id+"F7.wireOp",EDGE,"E10"),sQuery(id+"F7.wireOp",EDGE,"E19"),sQuery(id+"F7.wireOp",EDGE,"E20")])]}),"instanceName":"9"});
            var Q60;
            Q60=makeQuery(id+"F1.opRevolve","SWEPT_BODY",BODY,{"disambiguationData":[OSD([sQuery(id+"F0.wireOp",EDGE,"E0"),sQuery(id+"F0.wireOp",EDGE,"E1"),sQuery(id+"F0.wireOp",EDGE,"E2"),sQuery(id+"F0.wireOp",EDGE,"E3"),sQuery(id+"F0.wireOp",EDGE,"E4")])]});
            booleanBodies(context, id + "F10", {"operationType" : BooleanOperationType.SUBTRACTION, "tools" : qUnion([Q0, Q1, Q2, Q3, Q4, Q5, Q6, Q7, Q8, Q9, Q10, Q11, Q12, Q13, Q14, Q15, Q16, Q17, Q18, Q19, Q20, Q21, Q22, Q23, Q24, Q25, Q26, Q27, Q28, Q29, Q30, Q31, Q32, Q33, Q34, Q35, Q36, Q37, Q38, Q39, Q40, Q41, Q42, Q43, Q44, Q45, Q46, Q47, Q48, Q49, Q50, Q51, Q52, Q53, Q54, Q55, Q56, Q57, Q58, Q59]), "targets" : qUnion([Q60])});
        }
        {
            var Q0;
            Q0=makeQuery(id+"F1.opRevolve","SWEPT_FACE",FACE,{"disambiguationData":[OSD([sQuery(id+"F0.wireOp",EDGE,"E1")])]});
            var sketch = newSketch(context, id + "F11", { "sketchPlane" : qUnion([Q0])});
            skCircle(sketch, "E23", {"center": v(-10.16, -10.16) * mm, "radius": 3.18 * mm});
            skCircle(sketch, "E24", {"center": v(-10.16, 10.16) * mm, "radius": 3.18 * mm});
            skCircle(sketch, "E25", {"center": v(10.16, -10.16) * mm, "radius": 3.18 * mm});
            skCircle(sketch, "E26", {"center": v(10.16, 10.16) * mm, "radius": 3.18 * mm});
            skSolve(sketch);
        }
        {
            var Q0;
            {Q0=qUnion([makeQuery(id+"F11.imprint","IMPRINT",FACE,{"disambiguationData":[TD([[makeQuery(id+"F11.imprint","IMPRINT",EDGE,{"derivedFrom":sQuery(id+"F11.wireOp",EDGE,"E23")}),1.0]])]}),makeQuery(id+"F11.imprint","IMPRINT",FACE,{"disambiguationData":[TD([[makeQuery(id+"F11.imprint","IMPRINT",EDGE,{"derivedFrom":sQuery(id+"F11.wireOp",EDGE,"E24")}),1.0]])]}),makeQuery(id+"F11.imprint","IMPRINT",FACE,{"disambiguationData":[TD([[makeQuery(id+"F11.imprint","IMPRINT",EDGE,{"derivedFrom":sQuery(id+"F11.wireOp",EDGE,"E25")}),1.0]])]}),makeQuery(id+"F11.imprint","IMPRINT",FACE,{"disambiguationData":[TD([[makeQuery(id+"F11.imprint","IMPRINT",EDGE,{"derivedFrom":sQuery(id+"F11.wireOp",EDGE,"E26")}),1.0]])]})]);}
            extrude(context, id + "F12", {"entities" : qUnion([Q0]), "operationType" : NewBodyOperationType.REMOVE, "endBound" : BoundingType.THROUGH_ALL, "oppositeDirection" : true, "depth" : 25.4 * mm});
        }
        {
            var Q0;
            Q0=makeQuery(id+"F10.opBoolean","COPY",EDGE,{"derivedFrom":makeQuery(id+"F8.opExtrude","SWEPT_EDGE",EDGE,{"disambiguationData":[OSD([sQuery(id+"F7.wireOp",EDGE,"E9"),sQuery(id+"F7.wireOp",EDGE,"E22")])]})});
            var Q1;
            Q1=makeQuery(id+"F10.opBoolean","COPY",EDGE,{"derivedFrom":makeQuery(id+"F8.opExtrude","SWEPT_EDGE",EDGE,{"disambiguationData":[OSD([sQuery(id+"F7.wireOp",EDGE,"E9"),sQuery(id+"F7.wireOp",EDGE,"E20")])]})});
            var Q2;
            Q2=makeQuery(id+"F10.opBoolean","COPY",EDGE,{"derivedFrom":makeQuery(id+"F8.opExtrude","SWEPT_EDGE",EDGE,{"disambiguationData":[OSD([sQuery(id+"F7.wireOp",EDGE,"E9"),sQuery(id+"F7.wireOp",EDGE,"E18")])]})});
            var Q3;
            Q3=makeQuery(id+"F10.opBoolean","COPY",EDGE,{"derivedFrom":makeQuery(id+"F8.opExtrude","SWEPT_EDGE",EDGE,{"disambiguationData":[OSD([sQuery(id+"F7.wireOp",EDGE,"E9"),sQuery(id+"F7.wireOp",EDGE,"E16")])]})});
            var Q4;
            Q4=makeQuery(id+"F10.opBoolean","COPY",EDGE,{"derivedFrom":makeQuery(id+"F8.opExtrude","SWEPT_EDGE",EDGE,{"disambiguationData":[OSD([sQuery(id+"F7.wireOp",EDGE,"E9"),sQuery(id+"F7.wireOp",EDGE,"E14")])]})});
            var Q5;
            Q5=makeQuery(id+"F10.opBoolean","COPY",EDGE,{"derivedFrom":makeQuery(id+"F8.opExtrude","SWEPT_EDGE",EDGE,{"disambiguationData":[OSD([sQuery(id+"F7.wireOp",EDGE,"E9"),sQuery(id+"F7.wireOp",EDGE,"E12")])]})});
            var Q6;
            Q6=makeQuery(id+"F10.opBoolean","COPY",EDGE,{"derivedFrom":makeQuery(id+"F8.opExtrude","SWEPT_EDGE",EDGE,{"disambiguationData":[OSD([sQuery(id+"F7.wireOp",EDGE,"E10"),sQuery(id+"F7.wireOp",EDGE,"E22")])]})});
            var Q7;
            Q7=makeQuery(id+"F10.opBoolean","COPY",EDGE,{"derivedFrom":makeQuery(id+"F8.opExtrude","SWEPT_EDGE",EDGE,{"disambiguationData":[OSD([sQuery(id+"F7.wireOp",EDGE,"E10"),sQuery(id+"F7.wireOp",EDGE,"E20")])]})});
            var Q8;
            Q8=makeQuery(id+"F10.opBoolean","COPY",EDGE,{"derivedFrom":makeQuery(id+"F8.opExtrude","SWEPT_EDGE",EDGE,{"disambiguationData":[OSD([sQuery(id+"F7.wireOp",EDGE,"E10"),sQuery(id+"F7.wireOp",EDGE,"E18")])]})});
            var Q9;
            Q9=makeQuery(id+"F10.opBoolean","COPY",EDGE,{"derivedFrom":makeQuery(id+"F8.opExtrude","SWEPT_EDGE",EDGE,{"disambiguationData":[OSD([sQuery(id+"F7.wireOp",EDGE,"E10"),sQuery(id+"F7.wireOp",EDGE,"E16")])]})});
            var Q10;
            Q10=makeQuery(id+"F10.opBoolean","COPY",EDGE,{"derivedFrom":makeQuery(id+"F8.opExtrude","SWEPT_EDGE",EDGE,{"disambiguationData":[OSD([sQuery(id+"F7.wireOp",EDGE,"E10"),sQuery(id+"F7.wireOp",EDGE,"E14")])]})});
            var Q11;
            Q11=makeQuery(id+"F10.opBoolean","COPY",EDGE,{"derivedFrom":makeQuery(id+"F8.opExtrude","SWEPT_EDGE",EDGE,{"disambiguationData":[OSD([sQuery(id+"F7.wireOp",EDGE,"E10"),sQuery(id+"F7.wireOp",EDGE,"E12")])]})});
            fillet(context, id + "F13", {"entities" : qUnion([Q0, Q1, Q2, Q3, Q4, Q5, Q6, Q7, Q8, Q9, Q10, Q11]), "radius" : 5.08 * mm, "tangentPropagation" : true, "allowEdgeOverflow" : false});
        }
        {
            var Q0;
            Q0=makeQuery(id+"F13.opFillet","BLEND_EDGE",EDGE,{"blendedFrom":[makeQuery(id+"F10.opBoolean","COPY",EDGE,{"derivedFrom":makeQuery(id+"F8.opExtrude","SWEPT_EDGE",EDGE,{"disambiguationData":[OSD([sQuery(id+"F7.wireOp",EDGE,"E9"),sQuery(id+"F7.wireOp",EDGE,"E22")])]})}),makeQuery(id+"F1.opRevolve","SWEPT_FACE",FACE,{"disambiguationData":[OSD([sQuery(id+"F0.wireOp",EDGE,"E2")])]})],"blendedInto":[makeQuery(id+"F1.opRevolve","SWEPT_FACE",FACE,{"disambiguationData":[OSD([sQuery(id+"F0.wireOp",EDGE,"E2")])]})]});
            fillet(context, id + "F14", {"entities" : qUnion([Q0]), "radius" : 8.38 * mm, "tangentPropagation" : true, "allowEdgeOverflow" : false});
        }
        {
            var Q0;
            Q0=makeQuery(id+"F10.opBoolean","INTERSECT",EDGE,{"derivedFrom":[makeQuery(id+"F1.opRevolve","SWEPT_FACE",FACE,{"disambiguationData":[OSD([sQuery(id+"F0.wireOp",EDGE,"E2")])]}),makeQuery(id+"F8.opExtrude","SWEPT_FACE",FACE,{"disambiguationData":[OSD([sQuery(id+"F7.wireOp",EDGE,"E20")])]})]});
            fillet(context, id + "F15", {"entities" : qUnion([Q0]), "radius" : 3.8 * mm, "tangentPropagation" : true, "allowEdgeOverflow" : false});
        }
    });
